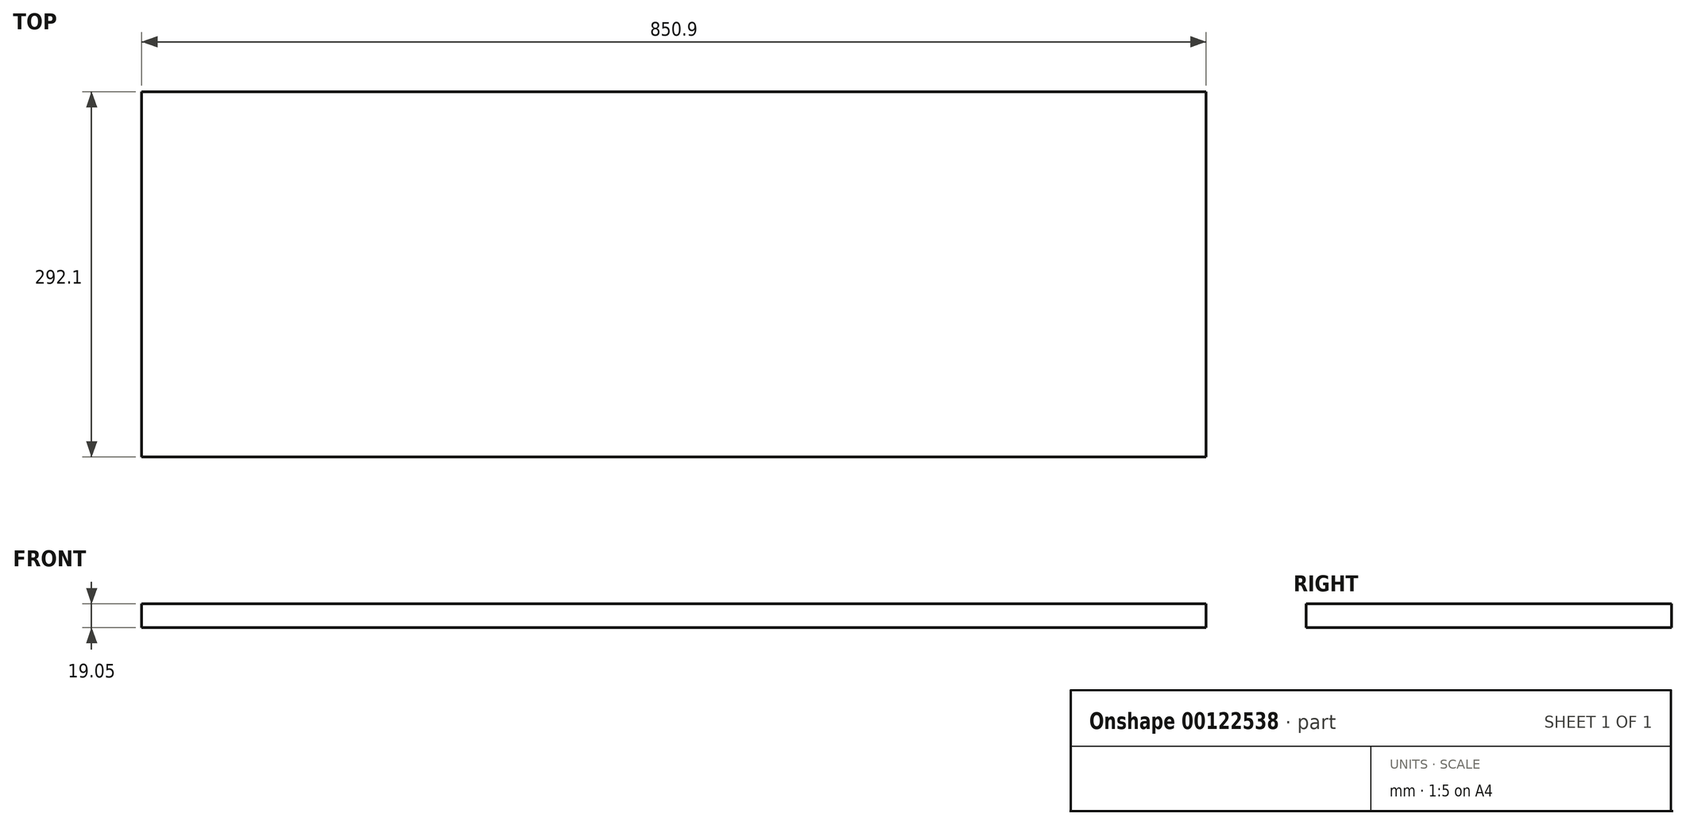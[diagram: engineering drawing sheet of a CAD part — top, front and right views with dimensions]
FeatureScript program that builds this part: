
annotation { "Feature Type Name" : "Feature", "Feature Type Description" : "" }
export const myFeature = defineFeature(function(context is Context, id is Id, definition is map)
    precondition{}
    {
        {
            var Q0;
            Q0=qCreatedBy(makeId("Top.planeOp"),FACE);
            var sketch = newSketch(context, id + "F0", { "sketchPlane" : qUnion([Q0])});
            skLineSegment(sketch, "E0.bottom", {"start": v(-425.45, 146.05) * mm, "end": v(425.45, 146.05) * mm});
            skLineSegment(sketch, "E0.top", {"start": v(-425.45, -146.05) * mm, "end": v(425.45, -146.05) * mm});
            skLineSegment(sketch, "E0.left", {"start": v(-425.45, 146.05) * mm, "end": v(-425.45, -146.05) * mm});
            skLineSegment(sketch, "E0.right", {"start": v(425.45, 146.05) * mm, "end": v(425.45, -146.05) * mm});
            skPoint(sketch, "E0.middle", {"position": v(0, 0) * mm});
            skSolve(sketch);
        }
        {
            var Q0;
            Q0=makeQuery(id+"F0.imprint","IMPRINT",FACE,{"disambiguationData":[TD([[makeQuery(id+"F0.imprint","IMPRINT",EDGE,{"derivedFrom":sQuery(id+"F0.wireOp",EDGE,"E0.bottom")}),-1.0]])]});
            extrude(context, id + "F1", {"entities" : qUnion([Q0]), "depth" : 19.05 * mm});
        }
    });
